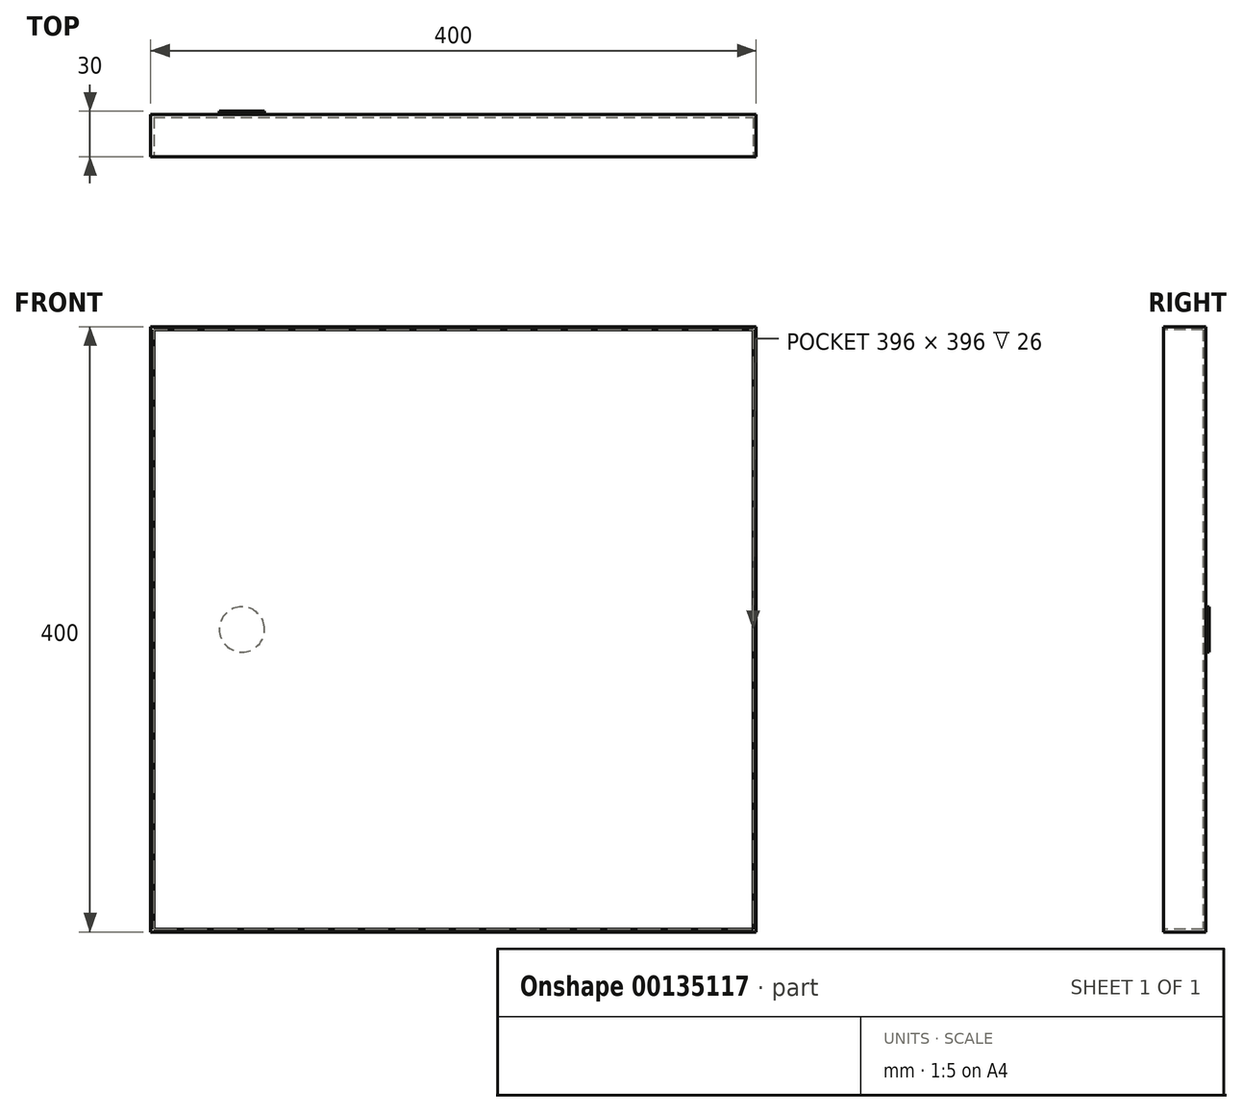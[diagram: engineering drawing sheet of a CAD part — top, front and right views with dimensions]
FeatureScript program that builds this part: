
annotation { "Feature Type Name" : "Feature", "Feature Type Description" : "" }
export const myFeature = defineFeature(function(context is Context, id is Id, definition is map)
    precondition{}
    {
        {
            var Q0;
            Q0=qCreatedBy(makeId("Front.planeOp"),FACE);
            var sketch = newSketch(context, id + "F0", { "sketchPlane" : qUnion([Q0])});
            skLineSegment(sketch, "E0.bottom", {"start": v(-354.3, 366.6) * mm, "end": v(45.7, 366.6) * mm});
            skLineSegment(sketch, "E0.top", {"start": v(-354.3, -33.4) * mm, "end": v(45.7, -33.4) * mm});
            skLineSegment(sketch, "E0.left", {"start": v(-354.3, 366.6) * mm, "end": v(-354.3, -33.4) * mm});
            skLineSegment(sketch, "E0.right", {"start": v(45.7, 366.6) * mm, "end": v(45.7, -33.4) * mm});
            skSolve(sketch);
        }
        {
            var Q0;
            Q0=makeQuery(id+"F0.imprint","IMPRINT",FACE,{"disambiguationData":[TD([[makeQuery(id+"F0.imprint","IMPRINT",EDGE,{"derivedFrom":sQuery(id+"F0.wireOp",EDGE,"E0.bottom")}),-1.0]])]});
            extrude(context, id + "F1", {"entities" : qUnion([Q0]), "depth" : 28 * mm});
        }
        {
            var Q0;
            Q0=makeQuery(id+"F1.opExtrude","CAP_FACE",FACE,{"disambiguationData":[OSD([sQuery(id+"F0.wireOp",EDGE,"E0.bottom"),sQuery(id+"F0.wireOp",EDGE,"E0.top"),sQuery(id+"F0.wireOp",EDGE,"E0.left"),sQuery(id+"F0.wireOp",EDGE,"E0.right")])],"isStart":false});
            var sketch = newSketch(context, id + "F2", { "sketchPlane" : qUnion([Q0])});
            skLineSegment(sketch, "E1.bottom", {"start": v(-352.3, 364.6) * mm, "end": v(43.7, 364.6) * mm});
            skLineSegment(sketch, "E1.top", {"start": v(-352.3, -31.4) * mm, "end": v(43.7, -31.4) * mm});
            skLineSegment(sketch, "E1.left", {"start": v(-352.3, 364.6) * mm, "end": v(-352.3, -31.4) * mm});
            skLineSegment(sketch, "E1.right", {"start": v(43.7, 364.6) * mm, "end": v(43.7, -31.4) * mm});
            skSolve(sketch);
        }
        {
            var Q0;
            Q0=makeQuery(id+"F2.imprint","IMPRINT",FACE,{"disambiguationData":[TD([[makeQuery(id+"F2.imprint","IMPRINT",EDGE,{"derivedFrom":sQuery(id+"F2.wireOp",EDGE,"E1.bottom")}),-1.0]])]});
            extrude(context, id + "F3", {"entities" : qUnion([Q0]), "operationType" : NewBodyOperationType.REMOVE, "oppositeDirection" : true, "depth" : 26 * mm});
        }
        {
            var Q0;
            Q0=makeQuery(id+"F1.opExtrude","CAP_FACE",FACE,{"disambiguationData":[OSD([sQuery(id+"F0.wireOp",EDGE,"E0.bottom"),sQuery(id+"F0.wireOp",EDGE,"E0.top"),sQuery(id+"F0.wireOp",EDGE,"E0.left"),sQuery(id+"F0.wireOp",EDGE,"E0.right")])],"isStart":true});
            var sketch = newSketch(context, id + "F4", { "sketchPlane" : qUnion([Q0])});
            skCircle(sketch, "E2", {"center": v(294.03, 166.6) * mm, "radius": 15 * mm});
            skPoint(sketch, "E2.centerSnap0", {"position": v(354.3, 166.6) * mm});
            skSolve(sketch);
        }
        {
            var Q0;
            Q0=makeQuery(id+"F4.imprint","IMPRINT",FACE,{"disambiguationData":[TD([[makeQuery(id+"F4.imprint","IMPRINT",EDGE,{"derivedFrom":sQuery(id+"F4.wireOp",EDGE,"E2")}),1.0]])]});
            extrude(context, id + "F5", {"entities" : qUnion([Q0]), "operationType" : NewBodyOperationType.ADD, "depth" : 2 * mm});
        }
    });
